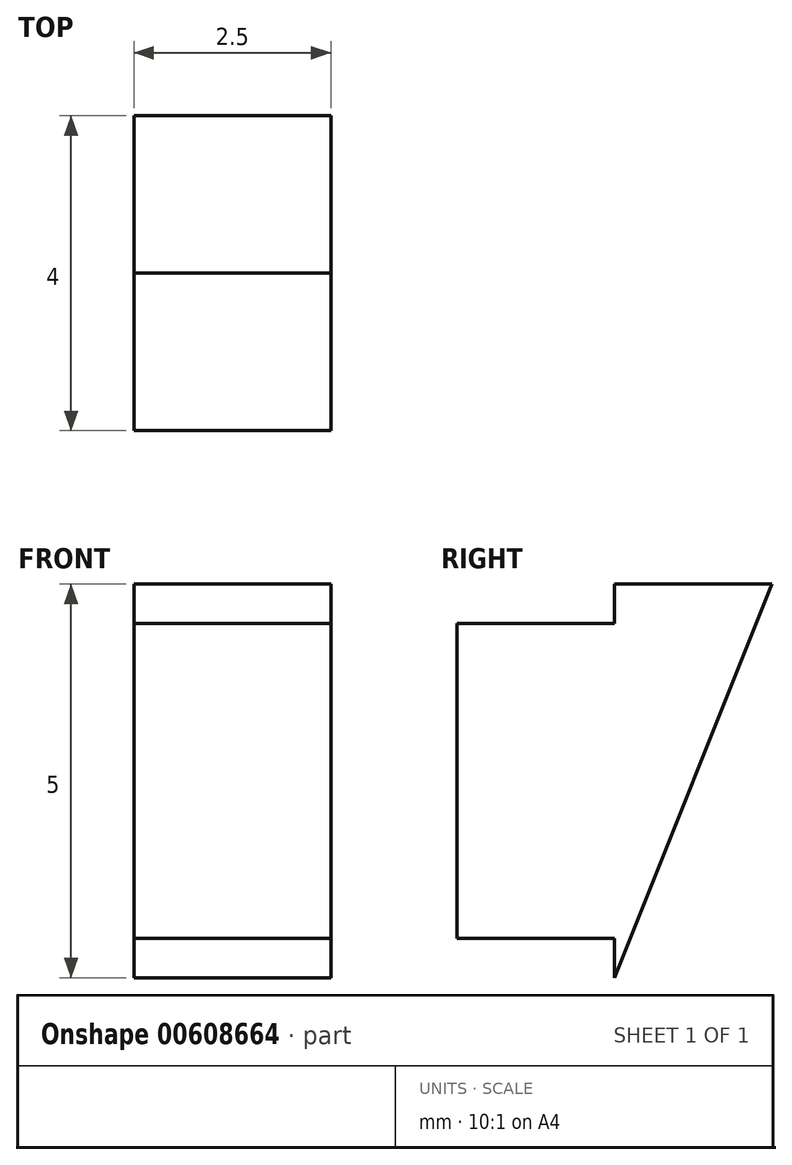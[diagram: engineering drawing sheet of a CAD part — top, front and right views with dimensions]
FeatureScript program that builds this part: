
annotation { "Feature Type Name" : "Feature", "Feature Type Description" : "" }
export const myFeature = defineFeature(function(context is Context, id is Id, definition is map)
    precondition{}
    {
        {
            var Q0;
            Q0=qCreatedBy(makeId("Right.planeOp"),FACE);
            var sketch = newSketch(context, id + "F0", { "sketchPlane" : qUnion([Q0])});
            skLineSegment(sketch, "E0.bottom", {"start": v(1, -2) * mm, "end": v(-1, -2) * mm});
            skLineSegment(sketch, "E0.top", {"start": v(1, 2) * mm, "end": v(-1, 2) * mm});
            skLineSegment(sketch, "E0.left", {"start": v(1, -2) * mm, "end": v(1, 2) * mm});
            skLineSegment(sketch, "E0.right", {"start": v(-1, -2) * mm, "end": v(-1, 2) * mm});
            skPoint(sketch, "E0.middle", {"position": v(0, 0) * mm});
            skLineSegment(sketch, "E1.bottom", {"start": v(3, -2.5) * mm, "end": v(1, -2.5) * mm});
            skLineSegment(sketch, "E1.top", {"start": v(3, 2.5) * mm, "end": v(1, 2.5) * mm});
            skLineSegment(sketch, "E1.left", {"start": v(3, -2.5) * mm, "end": v(3, 2.5) * mm});
            skLineSegment(sketch, "E1.right", {"start": v(1, -2.5) * mm, "end": v(1, 2.5) * mm});
            skPoint(sketch, "E1.middle", {"position": v(2, 0) * mm});
            skLineSegment(sketch, "E2", {"start": v(1, -2.5) * mm, "end": v(3, 2.5) * mm});
            skSolve(sketch);
        }
        {
            var Q0;
            {var subQ0=sQuery(id+"F0.wireOp",EDGE,"E0.bottom");Q0=makeQuery(id+"F0.imprint","IMPRINT",FACE,{"disambiguationData":[TD([[makeQuery(id+"F0.imprint","IMPRINT",EDGE,{"derivedFrom":subQ0}),-1.0]])]});}
            var Q1;
            {var subQ2=sQuery(id+"F0.wireOp",EDGE,"E1.top");Q1=makeQuery(id+"F0.imprint","IMPRINT",FACE,{"disambiguationData":[TD([[makeQuery(id+"F0.imprint","IMPRINT",EDGE,{"derivedFrom":subQ2}),1.0]])]});}
            extrude(context, id + "F1", {"entities" : qUnion([Q0, Q1]), "depth" : 2.5 * mm, "offsetDistance" : 25 * mm});
        }
    });
